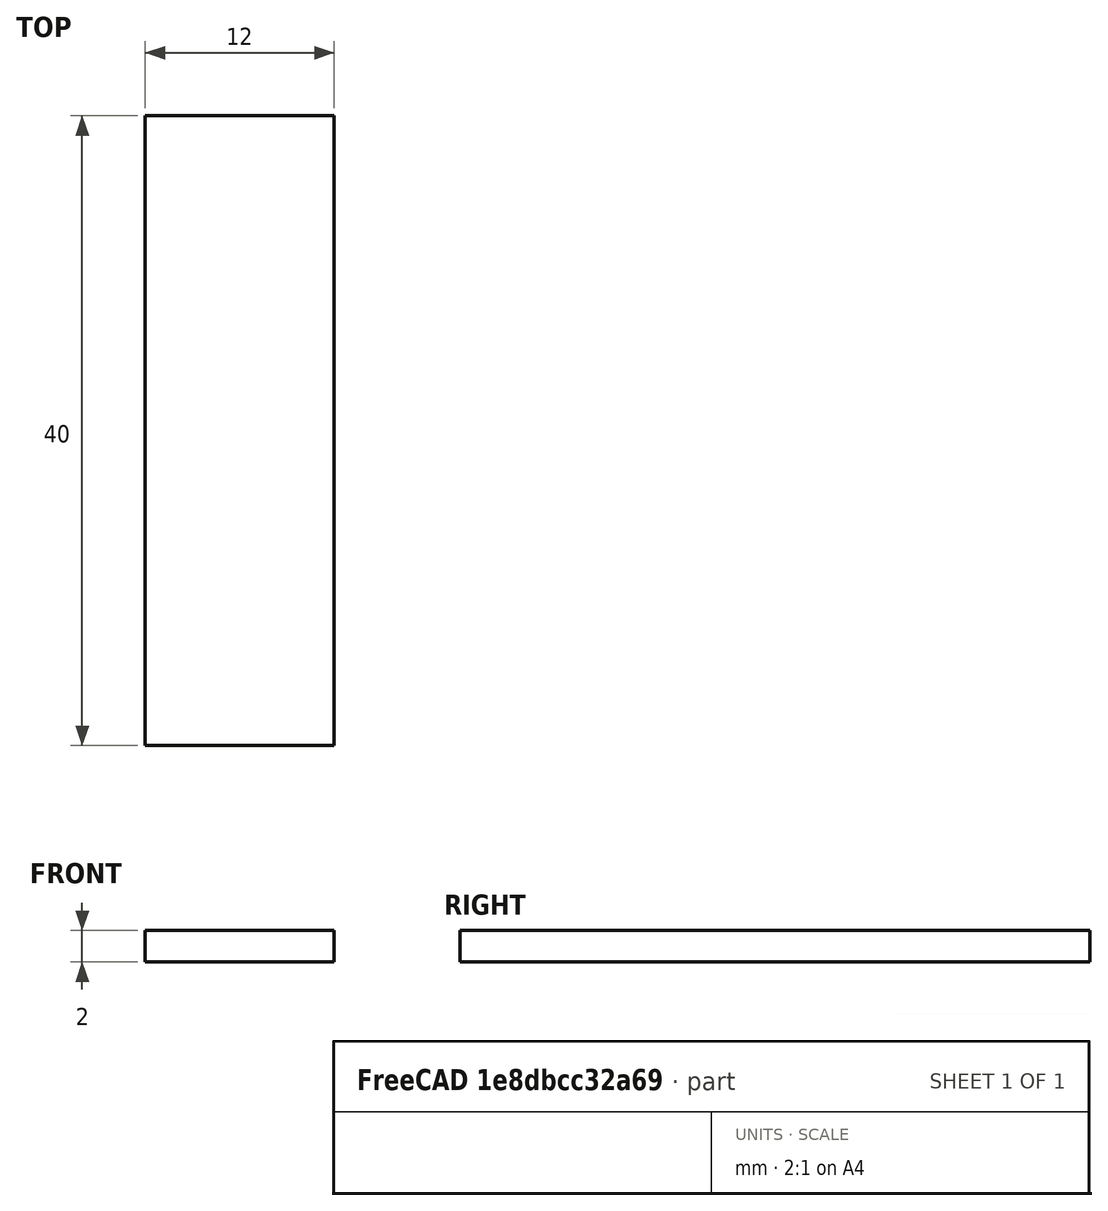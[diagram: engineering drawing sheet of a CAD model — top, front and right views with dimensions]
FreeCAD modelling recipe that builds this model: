
FCSTD DOCUMENT  (FreeCAD 0.20R29603 (Git))
Label: ConnectorBack
License: All rights reserved
LicenseURL: http://en.wikipedia.org/wiki/All_rights_reserved
objects: Sketcher::SketchObject×1, PartDesign::Pad×1, PartDesign::Body×1
note: 4 computed .brp shape members not serialized (recipe doc carries the construction recipe); baked Part::Feature solids carry a one-line shape summary decoded from their .brp

FEATURE [Sketcher::SketchObject] Sketch
  FullyConstrained = true
  MapMode = 5
  Support = -> [XY_Plane]
  sketch-geometry (5):
    g0: LineSegment StartX=-6 StartY=20 StartZ=0 EndX=-6 EndY=-20 EndZ=0
    g1: LineSegment StartX=-6 StartY=-20 StartZ=0 EndX=6 EndY=-20 EndZ=0
    g2: LineSegment StartX=6 StartY=-20 StartZ=0 EndX=6 EndY=20 EndZ=0
    g3: LineSegment StartX=6 StartY=20 StartZ=0 EndX=-6 EndY=20 EndZ=0
    g4: GeomPoint X=0 Y=0 Z=0
  constraints (12):
    c: Coincident(g0,g1)
    c: Coincident(g1,g2)
    c: Coincident(g2,g3)
    c: Coincident(g3,g0)
    c: Horizontal(g1)
    c: Horizontal(g3)
    c: Vertical(g0)
    c: Vertical(g2)
    c: Symmetric(g1,g0,g4)
    c: Coincident(g4,g-1)
    c: DistanceX(g3,g3) = 12
    c: DistanceY(g2,g2) = 40
FEATURE [PartDesign::Pad] Pad
  Direction = (0,0,1)
  Length = 2
  Length2 = 10
  Profile = -> Sketch
  ReferenceAxis = -> Sketch [N_Axis]
  Type = 0
FEATURE [PartDesign::Body] Body
  Group = -> [Sketch,Pad]
  Origin = -> Origin
  Tip = -> Pad
